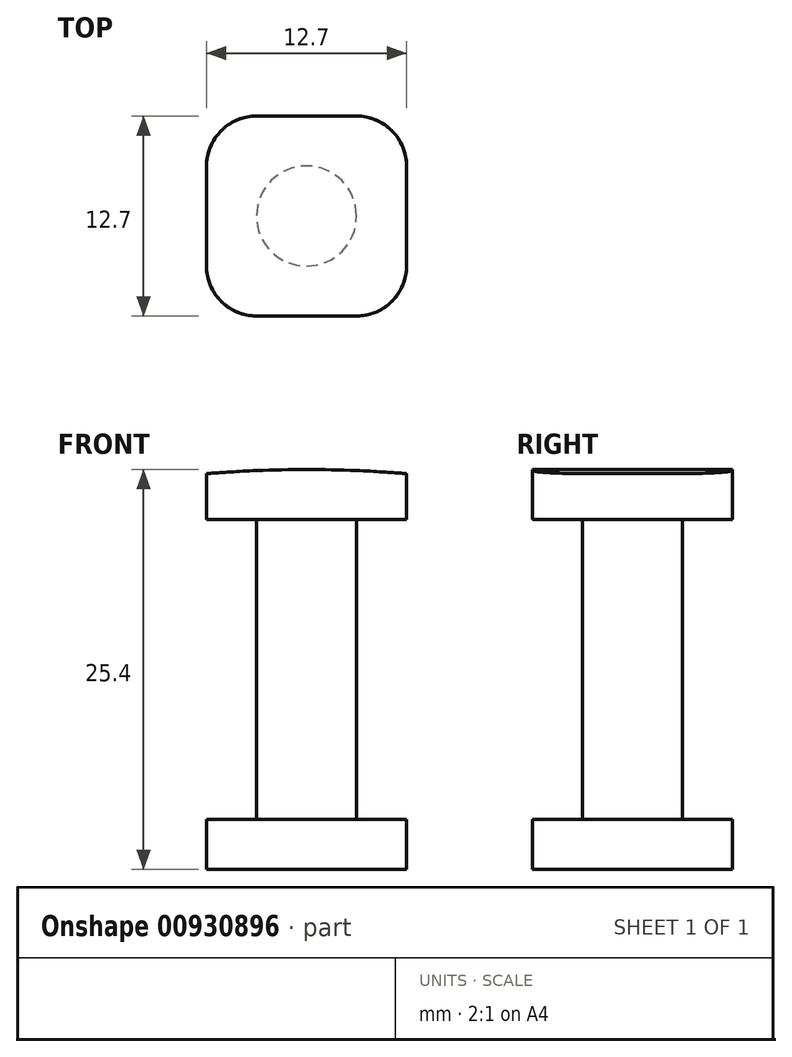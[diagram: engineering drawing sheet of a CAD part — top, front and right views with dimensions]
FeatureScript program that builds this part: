
annotation { "Feature Type Name" : "Feature", "Feature Type Description" : "" }
export const myFeature = defineFeature(function(context is Context, id is Id, definition is map)
    precondition{}
    {
        {
            var Q0;
            Q0=qCreatedBy(makeId("Top.planeOp"),FACE);
            var sketch = newSketch(context, id + "F0", { "sketchPlane" : qUnion([Q0])});
            skLineSegment(sketch, "E0.bottom", {"start": v(3.17, 6.35) * mm, "end": v(-3.18, 6.35) * mm});
            skLineSegment(sketch, "E0.top", {"start": v(3.18, -6.35) * mm, "end": v(-3.17, -6.35) * mm});
            skLineSegment(sketch, "E0.left", {"start": v(6.35, 3.18) * mm, "end": v(6.35, -3.18) * mm});
            skLineSegment(sketch, "E0.right", {"start": v(-6.35, 3.17) * mm, "end": v(-6.35, -3.18) * mm});
            skPoint(sketch, "E0.middle", {"position": v(0, 0) * mm});
            skPoint(sketch, "E1.visualSharp", {"position": v(-6.35, 6.35) * mm});
            skArc(sketch, "E1.filletArc", {"start": v(-3.18, 6.35) * mm, "mid": v(-5.42, 5.42) * mm, "end": v(-6.35, 3.17) * mm});
            skPoint(sketch, "E2.visualSharp", {"position": v(6.35, 6.35) * mm});
            skArc(sketch, "E2.filletArc", {"start": v(6.35, 3.18) * mm, "mid": v(5.42, 5.42) * mm, "end": v(3.17, 6.35) * mm});
            skPoint(sketch, "E3.visualSharp", {"position": v(6.35, -6.35) * mm});
            skArc(sketch, "E3.filletArc", {"start": v(3.18, -6.35) * mm, "mid": v(5.42, -5.42) * mm, "end": v(6.35, -3.18) * mm});
            skPoint(sketch, "E4.visualSharp", {"position": v(-6.35, -6.35) * mm});
            skArc(sketch, "E4.filletArc", {"start": v(-6.35, -3.18) * mm, "mid": v(-5.42, -5.42) * mm, "end": v(-3.17, -6.35) * mm});
            skSolve(sketch);
        }
        {
            var Q0;
            Q0 = qSketchRegion(id + "F0", true);
            extrude(context, id + "F1", {"entities" : qUnion([Q0]), "depth" : 25.4 * mm, "offsetDistance" : 25.4 * mm});
        }
        {
            var Q0;
            Q0=makeQuery(id+"F1.opExtrude","SWEPT_FACE",FACE,{"disambiguationData":[OSD([sQuery(id+"F0.wireOp",EDGE,"E0.top")])]});
            cPlane(context, id + "F2", {"entities" : qUnion([Q0]), "cplaneType" : CPlaneType.OFFSET, "offset" : 0 * mm, "width" : 152.4 * mm, "height" : 152.4 * mm});
        }
        {
            var Q0;
            Q0=qCreatedBy(id+"F2.planeOp",FACE);
            var sketch = newSketch(context, id + "F3", { "sketchPlane" : qUnion([Q0])});
            skArc(sketch, "E5", {"start": v(46.27, 9.74) * mm, "mid": v(1.86, 25.38) * mm, "end": v(-43.26, 11.93) * mm});
            skLineSegment(sketch, "E6", {"start": v(-43.26, 11.93) * mm, "end": v(-43.26, 53.56) * mm});
            skLineSegment(sketch, "E7", {"start": v(-43.26, 53.56) * mm, "end": v(46.19, 53.56) * mm});
            skLineSegment(sketch, "E8", {"start": v(46.19, 53.56) * mm, "end": v(46.27, 9.74) * mm});
            skSolve(sketch);
        }
        {
            var Q0;
            Q0=makeQuery(id+"F3.imprint","IMPRINT",FACE,{"disambiguationData":[TD([[makeQuery(id+"F3.imprint","IMPRINT",EDGE,{"derivedFrom":sQuery(id+"F3.wireOp",EDGE,"E5")}),-1.0]])]});
            extrude(context, id + "F4", {"entities" : qUnion([Q0]), "operationType" : NewBodyOperationType.REMOVE, "oppositeDirection" : true, "depth" : 25.4 * mm, "offsetDistance" : 25.4 * mm});
        }
        {
            var Q0;
            Q0=qCreatedBy(id+"F2.planeOp",FACE);
            var sketch = newSketch(context, id + "F5", { "sketchPlane" : qUnion([Q0])});
            skCircle(sketch, "E9", {"center": v(0, -50.8) * mm, "radius": 50.8 * mm});
            skSolve(sketch);
        }
        {
            var Q0;
            Q0=makeQuery(id+"F5.imprint","IMPRINT",FACE,{"disambiguationData":[TD([[makeQuery(id+"F5.imprint","IMPRINT",EDGE,{"derivedFrom":sQuery(id+"F5.wireOp",EDGE,"E9")}),1.0]])]});
            extrude(context, id + "F6", {"entities" : qUnion([Q0]), "operationType" : NewBodyOperationType.REMOVE, "oppositeDirection" : true, "depth" : 25.4 * mm, "offsetDistance" : 25.4 * mm});
        }
        {
            var Q0;
            Q0=qCreatedBy(makeId("Front.planeOp"),FACE);
            var sketch = newSketch(context, id + "F7", { "sketchPlane" : qUnion([Q0])});
            skLineSegment(sketch, "E10.bottom", {"start": v(15, 22.23) * mm, "end": v(3.18, 22.23) * mm});
            skLineSegment(sketch, "E10.top", {"start": v(15, 3.18) * mm, "end": v(3.18, 3.18) * mm});
            skLineSegment(sketch, "E10.left", {"start": v(15, 22.23) * mm, "end": v(15, 3.18) * mm});
            skLineSegment(sketch, "E10.right", {"start": v(3.18, 22.23) * mm, "end": v(3.18, 3.18) * mm});
            skLineSegment(sketch, "E11", {"start": v(0, 42.66) * mm, "end": v(0, -3.16) * mm});
            skSolve(sketch);
        }
        {
            var Q0;
            Q0=makeQuery(id+"F7.imprint","IMPRINT",FACE,{"disambiguationData":[TD([[makeQuery(id+"F7.imprint","IMPRINT",EDGE,{"derivedFrom":sQuery(id+"F7.wireOp",EDGE,"E10.bottom")}),1.0]])]});
            var Q1;
            Q1=sQuery(id+"F7.wireOp",EDGE,"E11");
            revolve(context, id + "F8", {"operationType" : NewBodyOperationType.REMOVE, "surfaceOperationType" : NewSurfaceOperationType.NEW, "entities" : qUnion([Q0]), "axis" : qUnion([Q1]), "revolveType" : RevolveType.FULL, "oppositeDirection" : true});
        }
    });
